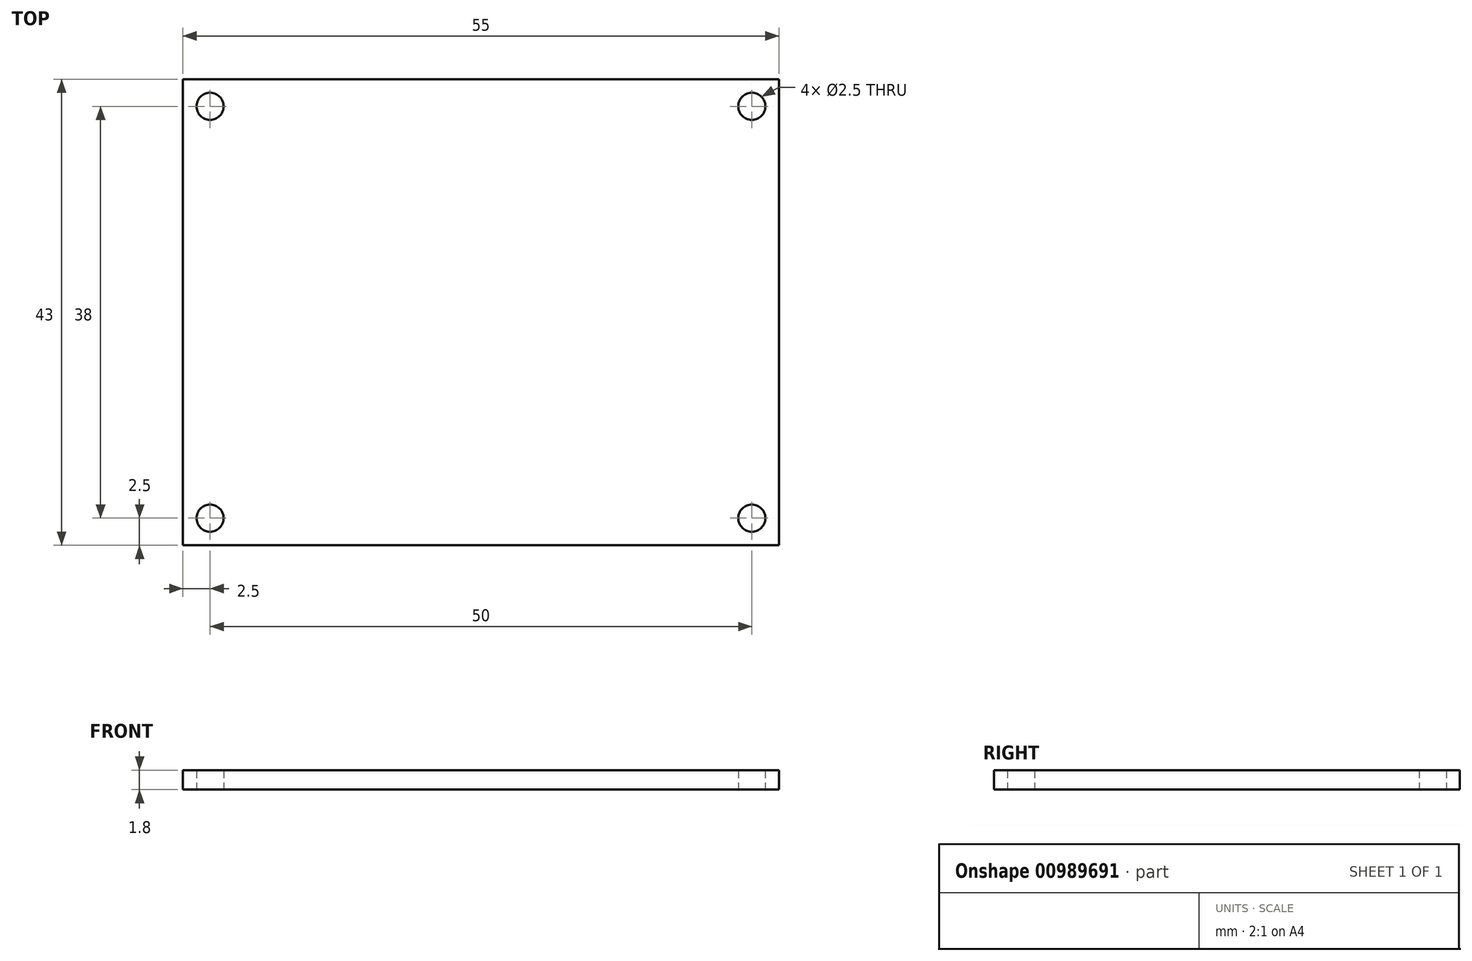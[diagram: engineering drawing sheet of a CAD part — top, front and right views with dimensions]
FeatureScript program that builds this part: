
annotation { "Feature Type Name" : "Feature", "Feature Type Description" : "" }
export const myFeature = defineFeature(function(context is Context, id is Id, definition is map)
    precondition{}
    {
        {
            var Q0;
            Q0=qCreatedBy(makeId("Top.planeOp"),FACE);
            var sketch = newSketch(context, id + "F0", { "sketchPlane" : qUnion([Q0])});
            skLineSegment(sketch, "E0.bottom", {"start": v(27.5, -21.5) * mm, "end": v(-27.5, -21.5) * mm});
            skLineSegment(sketch, "E0.top", {"start": v(27.5, 21.5) * mm, "end": v(-27.5, 21.5) * mm});
            skLineSegment(sketch, "E0.left", {"start": v(27.5, -21.5) * mm, "end": v(27.5, 21.5) * mm});
            skLineSegment(sketch, "E0.right", {"start": v(-27.5, -21.5) * mm, "end": v(-27.5, 21.5) * mm});
            skPoint(sketch, "E0.middle", {"position": v(0, 0) * mm});
            skCircle(sketch, "E1", {"center": v(-25, 19) * mm, "radius": 1.25 * mm});
            skCircle(sketch, "E2", {"center": v(-25, -19) * mm, "radius": 1.25 * mm});
            skCircle(sketch, "E3", {"center": v(25, 19) * mm, "radius": 1.25 * mm});
            skCircle(sketch, "E4", {"center": v(25, -19) * mm, "radius": 1.25 * mm});
            skSolve(sketch);
        }
        {
            var Q0;
            Q0=makeQuery(id+"F0.imprint","IMPRINT",FACE,{"disambiguationData":[TD([[makeQuery(id+"F0.imprint","IMPRINT",EDGE,{"derivedFrom":sQuery(id+"F0.wireOp",EDGE,"E0.bottom")}),-1.0]])]});
            extrude(context, id + "F1", {"entities" : qUnion([Q0]), "depth" : 1.8 * mm, "offsetDistance" : 25 * mm});
        }
    });
